# Revit family: DLB090028
name_source: partatom
category: Appareils sanitaires
revit_build: Autodesk Revit 2015 (Build: 20140606_1530(x64)
units: mm (PartAtom-declared; Revit-internal decimal feet)

## types (1)
- Type 1
    Category = Washbasin
    Description = French manufacturer Delabie is a leader in the European sanitary ware market for non-domestic places. Water controls, solutions for disabled people, sanitary ware, for schools, leisure centres, offices, hospitals, airports…
    Fabricant = DELABIE
    Features = Wall-mounted triple washbasin, 1,800 x 500mm. With an upstand to protect the wall from splashing and improve hygiene. Basin internal diameter: 310mm. Bacteriostatic 304 stainless steel. Stainless steel thickness: 1.5mm. Rounded edges prevent injury. Supplied with 1¼" waste. Without overflow. Supplied with brackets and fixing elements. CE marked. Complies with European standard EN 14688. Weight: 22kg.
    Finish = Polished satin
    Grade = CE
    ManufacturerName = DELABIE
    Material = 304 stainless steel
    Model number = 121750
    Modèle = TRIPLO RP
    Name = 121750
    NominalHeight = 26.5cm
    NominalLength = 50cm
    NominalWidth = 180cm
    Polantis code = DLB090028
    ProductInformation = http://www.delabie.com
    Radius = 42 mm
    SerialNumber = 3456330156639
    URL = http://www.delabie.com
    WarrantyDescription = Any manufacturing defect
    WarrantyDurationUnit = 10 years
    Weight = 22kg

## geometry (parser evidence)
native form markers: Sweep x3
no freeform markers — native parametric forms only
